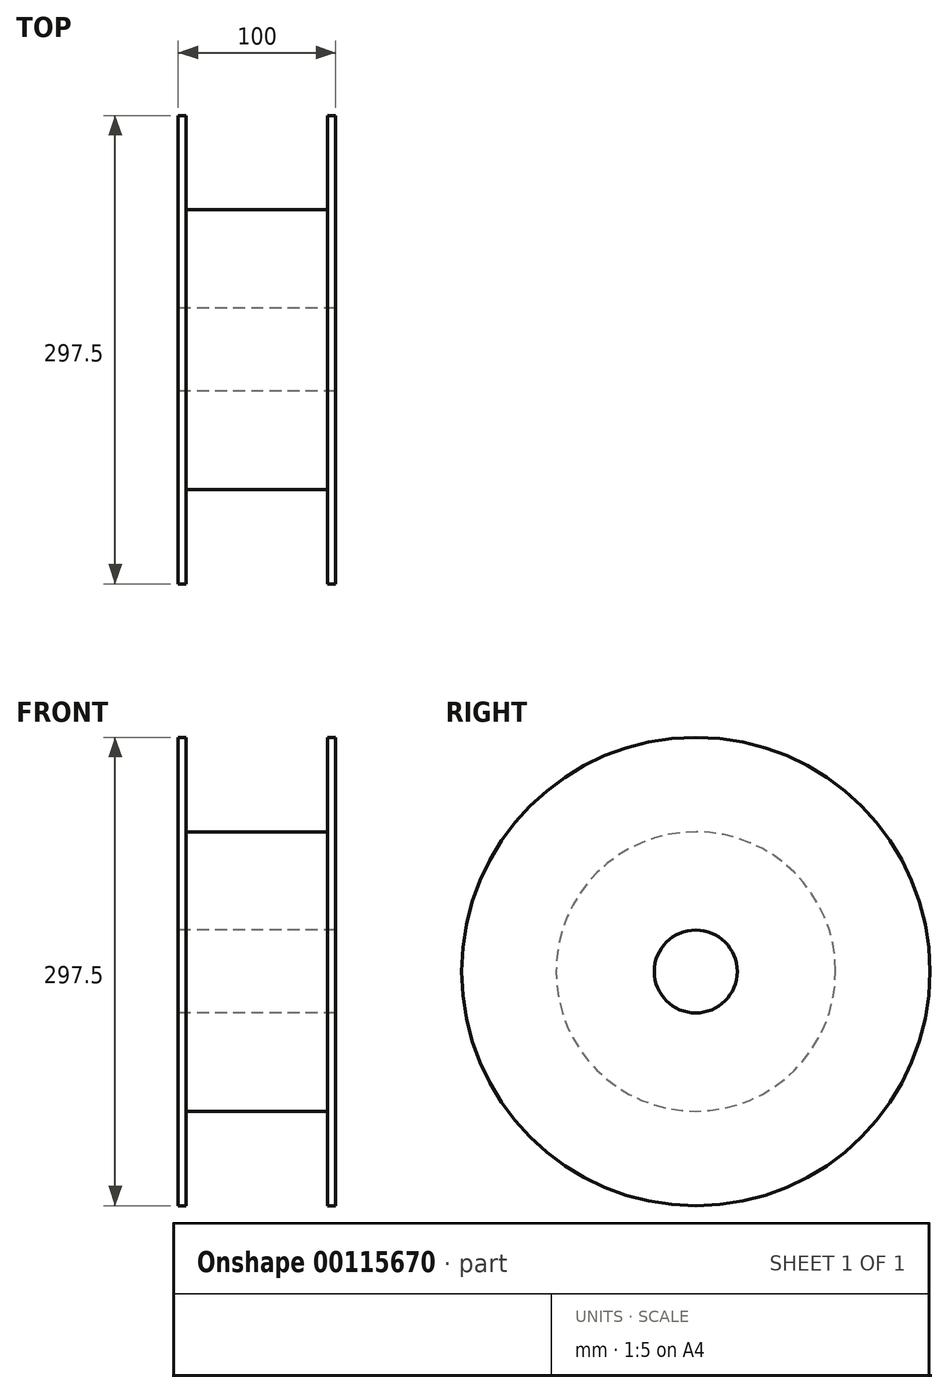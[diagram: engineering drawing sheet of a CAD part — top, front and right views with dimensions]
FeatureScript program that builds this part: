
annotation { "Feature Type Name" : "Feature", "Feature Type Description" : "" }
export const myFeature = defineFeature(function(context is Context, id is Id, definition is map)
    precondition{}
    {
        {
            var Q0;
            Q0=qCreatedBy(makeId("Front.planeOp"),FACE);
            var sketch = newSketch(context, id + "F0", { "sketchPlane" : qUnion([Q0])});
            skLineSegment(sketch, "E0", {"start": v(-50, 26.35) * mm, "end": v(50, 26.35) * mm});
            skLineSegment(sketch, "E1", {"start": v(-50, 148.75) * mm, "end": v(50, 148.75) * mm});
            skPoint(sketch, "E2", {"position": v(0, 148.75) * mm});
            skPoint(sketch, "E3", {"position": v(0, 26.35) * mm});
            skLineSegment(sketch, "E4", {"start": v(-50, 26.35) * mm, "end": v(-50, 148.75) * mm});
            skLineSegment(sketch, "E5", {"start": v(50, 26.35) * mm, "end": v(50, 148.75) * mm});
            skPoint(sketch, "E6", {"position": v(-45, 148.75) * mm});
            skPoint(sketch, "E7", {"position": v(45, 148.75) * mm});
            skLineSegment(sketch, "E8", {"start": v(-45, 148.75) * mm, "end": v(-45, 88.75) * mm});
            skLineSegment(sketch, "E9", {"start": v(-45, 88.75) * mm, "end": v(45, 88.75) * mm});
            skLineSegment(sketch, "E10", {"start": v(45, 88.75) * mm, "end": v(45, 148.75) * mm});
            skLineSegment(sketch, "E11", {"start": v(-89.4, 0) * mm, "end": v(112.07, 0) * mm, "construction": true});
            skSolve(sketch);
        }
        {
            var Q0;
            Q0=makeQuery(id+"F0.imprint","IMPRINT",FACE,{"disambiguationData":[TD([[makeQuery(id+"F0.imprint","IMPRINT",EDGE,{"derivedFrom":sQuery(id+"F0.wireOp",EDGE,"E0")}),1.0]])]});
            var Q1;
            Q1=sQuery(id+"F0.wireOp",EDGE,"E11");
            revolve(context, id + "F1", {"entities" : qUnion([Q0]), "axis" : qUnion([Q1]), "revolveType" : RevolveType.FULL});
        }
    });
